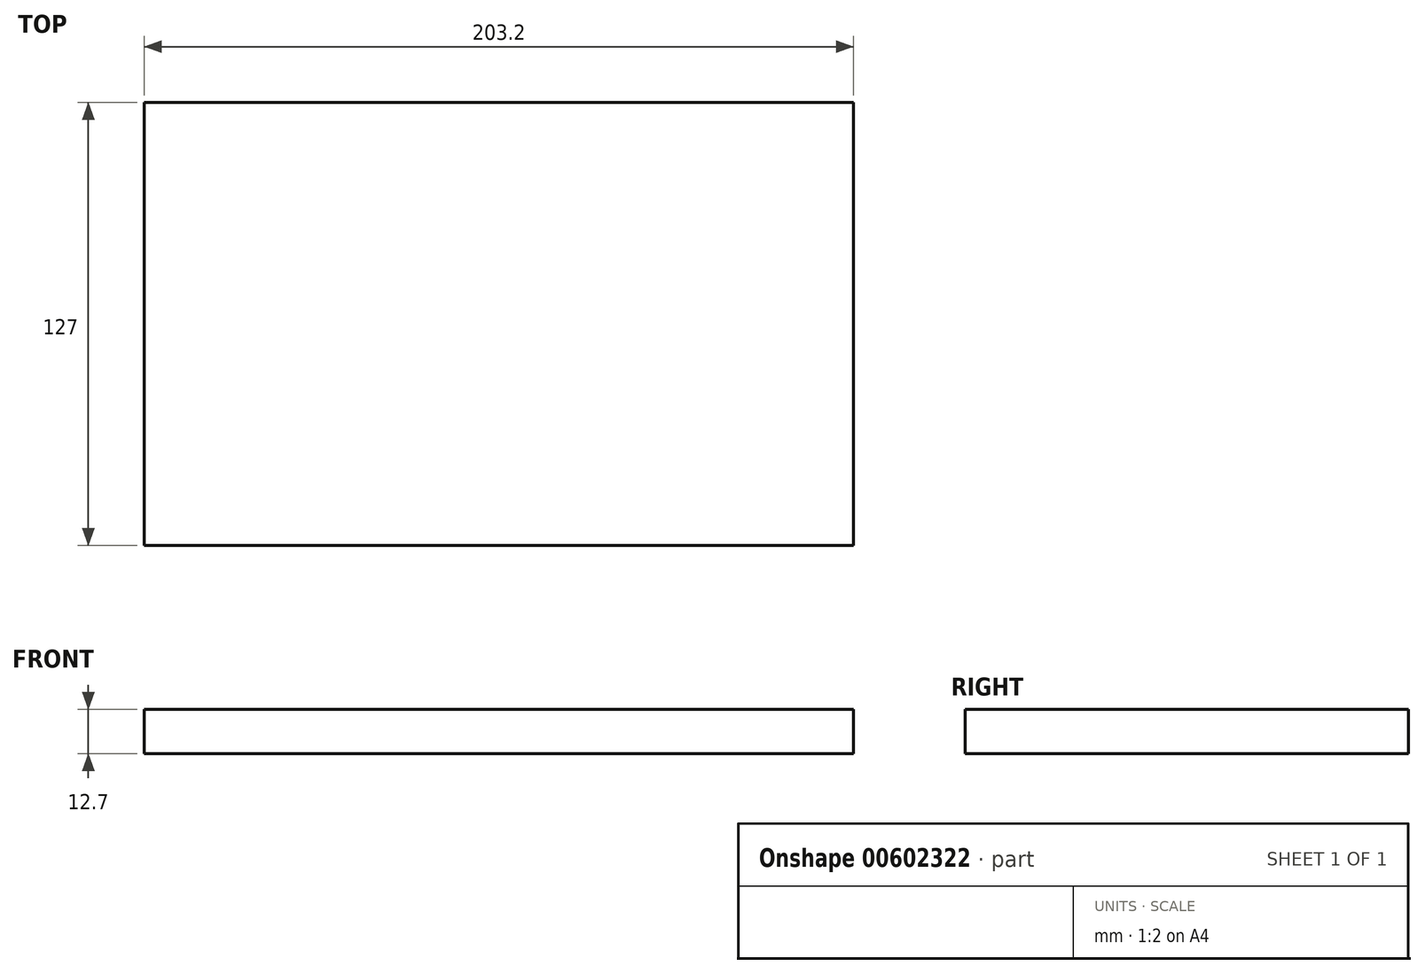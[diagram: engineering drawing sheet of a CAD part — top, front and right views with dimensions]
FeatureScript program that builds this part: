
annotation { "Feature Type Name" : "Feature", "Feature Type Description" : "" }
export const myFeature = defineFeature(function(context is Context, id is Id, definition is map)
    precondition{}
    {
        {
            var Q0;
            Q0=qCreatedBy(makeId("Top.planeOp"),FACE);
            var sketch = newSketch(context, id + "F0", { "sketchPlane" : qUnion([Q0])});
            skLineSegment(sketch, "E0.bottom", {"start": v(-101.6, 63.5) * mm, "end": v(101.6, 63.5) * mm});
            skLineSegment(sketch, "E0.top", {"start": v(-101.6, -63.5) * mm, "end": v(101.6, -63.5) * mm});
            skLineSegment(sketch, "E0.left", {"start": v(-101.6, 63.5) * mm, "end": v(-101.6, -63.5) * mm});
            skLineSegment(sketch, "E0.right", {"start": v(101.6, 63.5) * mm, "end": v(101.6, -63.5) * mm});
            skPoint(sketch, "E0.middle", {"position": v(0, 0) * mm});
            skSolve(sketch);
        }
        {
            var Q0;
            Q0=makeQuery(id+"F0.imprint","IMPRINT",FACE,{"disambiguationData":[TD([[makeQuery(id+"F0.imprint","IMPRINT",EDGE,{"derivedFrom":sQuery(id+"F0.wireOp",EDGE,"E0.bottom")}),-1.0]])]});
            extrude(context, id + "F1", {"entities" : qUnion([Q0]), "depth" : 12.7 * mm, "offsetDistance" : 25.4 * mm});
        }
    });
